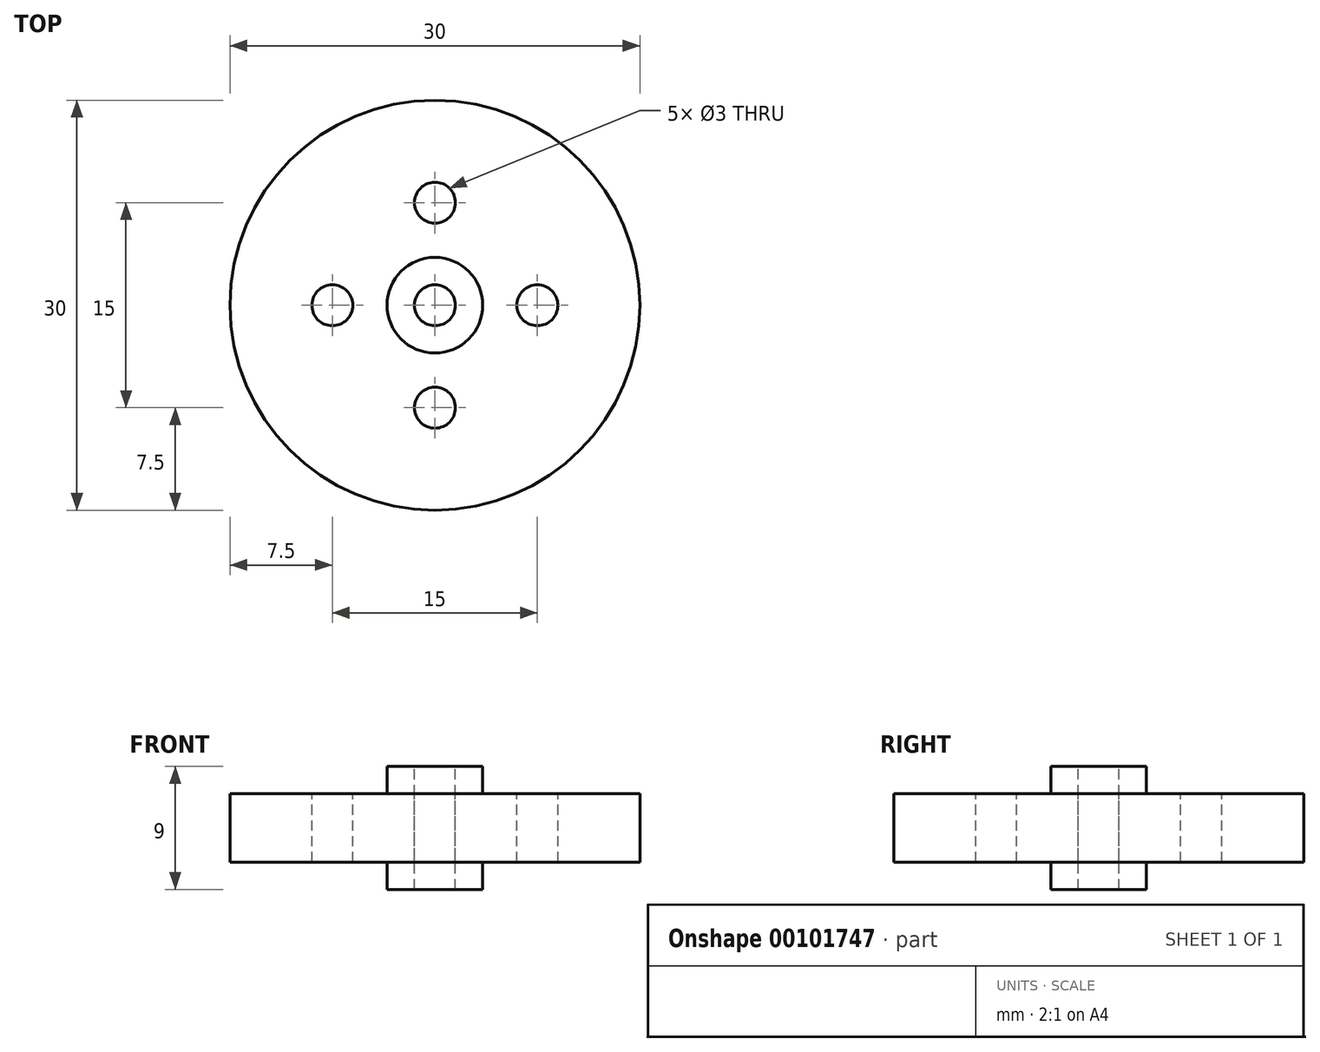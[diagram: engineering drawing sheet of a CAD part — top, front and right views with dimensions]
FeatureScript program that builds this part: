
annotation { "Feature Type Name" : "Feature", "Feature Type Description" : "" }
export const myFeature = defineFeature(function(context is Context, id is Id, definition is map)
    precondition{}
    {
        {
            var Q0;
            Q0=qCreatedBy(makeId("Top.planeOp"),FACE);
            var sketch = newSketch(context, id + "F0", { "sketchPlane" : qUnion([Q0])});
            skCircle(sketch, "E0", {"center": v(0, 0) * mm, "radius": 15 * mm});
            skSolve(sketch);
        }
        {
            var Q0;
            Q0=qSketchRegion(id+"F0",true);
            extrude(context, id + "F1", {"entities" : qUnion([Q0]), "depth" : 5 * mm});
        }
        {
            var Q0;
            Q0=makeQuery(id+"F1.opExtrude","CAP_FACE",FACE,{"disambiguationData":[OSD([sQuery(id+"F0.wireOp",EDGE,"E0")])],"isStart":false});
            var sketch = newSketch(context, id + "F2", { "sketchPlane" : qUnion([Q0])});
            skLineSegment(sketch, "E1", {"start": v(0, 15) * mm, "end": v(0, 7.5) * mm});
            skCircle(sketch, "E2", {"center": v(0, 7.5) * mm, "radius": 1.5 * mm});
            skCircle(sketch, "E3.1.0", {"center": v(-7.5, 0) * mm, "radius": 1.5 * mm});
            skCircle(sketch, "E3.2.0", {"center": v(0, -7.5) * mm, "radius": 1.5 * mm});
            skCircle(sketch, "E3.3.0", {"center": v(7.5, 0) * mm, "radius": 1.5 * mm});
            skPoint(sketch, "E3.center", {"position": v(0, 0) * mm});
            skCircle(sketch, "E4", {"center": v(0, 0) * mm, "radius": 3.5 * mm});
            skSolve(sketch);
        }
        {
            var Q0;
            Q0=makeQuery(id+"F2.imprint","IMPRINT",FACE,{"disambiguationData":[TD([[makeQuery(id+"F2.imprint","IMPRINT",EDGE,{"derivedFrom":sQuery(id+"F2.wireOp",EDGE,"E4")}),1.0]])]});
            extrude(context, id + "F3", {"entities" : qUnion([Q0]), "operationType" : NewBodyOperationType.ADD, "depth" : 2 * mm});
        }
        {
            var Q0;
            Q0=makeQuery(id+"F2.imprint","IMPRINT",FACE,{"disambiguationData":[TD([[makeQuery(id+"F2.imprint","IMPRINT",EDGE,{"derivedFrom":sQuery(id+"F2.wireOp",EDGE,"E2")}),1.0]])]});
            var Q1;
            Q1=makeQuery(id+"F2.imprint","IMPRINT",FACE,{"disambiguationData":[TD([[makeQuery(id+"F2.imprint","IMPRINT",EDGE,{"derivedFrom":sQuery(id+"F2.wireOp",EDGE,"E3.1.0")}),1.0]])]});
            var Q2;
            Q2=makeQuery(id+"F2.imprint","IMPRINT",FACE,{"disambiguationData":[TD([[makeQuery(id+"F2.imprint","IMPRINT",EDGE,{"derivedFrom":sQuery(id+"F2.wireOp",EDGE,"E3.2.0")}),1.0]])]});
            var Q3;
            Q3=makeQuery(id+"F2.imprint","IMPRINT",FACE,{"disambiguationData":[TD([[makeQuery(id+"F2.imprint","IMPRINT",EDGE,{"derivedFrom":sQuery(id+"F2.wireOp",EDGE,"E3.3.0")}),1.0]])]});
            extrude(context, id + "F4", {"entities" : qUnion([Q0, Q1, Q2, Q3]), "operationType" : NewBodyOperationType.REMOVE, "oppositeDirection" : true, "depth" : 5 * mm});
        }
        {
            var Q0;
            Q0=makeQuery(id+"F3.opExtrude","CAP_FACE",FACE,{"disambiguationData":[OSD([sQuery(id+"F2.wireOp",EDGE,"E4")])],"isStart":false});
            var sketch = newSketch(context, id + "F5", { "sketchPlane" : qUnion([Q0])});
            skCircle(sketch, "E5", {"center": v(0, 0) * mm, "radius": 1.5 * mm});
            skSolve(sketch);
        }
        {
            var Q0;
            Q0=makeQuery(id+"F5.imprint","IMPRINT",FACE,{"disambiguationData":[TD([[makeQuery(id+"F5.imprint","IMPRINT",EDGE,{"derivedFrom":sQuery(id+"F5.wireOp",EDGE,"E5")}),1.0]])]});
            extrude(context, id + "F6", {"entities" : qUnion([Q0]), "operationType" : NewBodyOperationType.REMOVE, "oppositeDirection" : true, "depth" : 10 * mm});
        }
        {
            var Q0;
            Q0=makeQuery(id+"F1.opExtrude","SWEPT_BODY",BODY,{"disambiguationData":[OSD([sQuery(id+"F0.wireOp",EDGE,"E0")])]});
            transform(context, id + "F7", {"entities" : qUnion([Q0]), "transformType" : TransformType.TRANSLATION_3D, "dx" : 0 * mm, "dy" : 0 * mm, "dz" : 0 * mm, "makeCopy" : true});
        }
        {
            var Q0;
            Q0=makeQuery(id+"F1.opExtrude","CAP_FACE",FACE,{"disambiguationData":[OSD([sQuery(id+"F0.wireOp",EDGE,"E0")])],"isStart":true});
            var sketch = newSketch(context, id + "F8", { "sketchPlane" : qUnion([Q0])});
            skCircle(sketch, "E6", {"center": v(0, 0) * mm, "radius": 3.5 * mm});
            skSolve(sketch);
        }
        {
            var Q0;
            Q0=makeQuery(id+"F8.imprint","IMPRINT",FACE,{"disambiguationData":[TD([[makeQuery(id+"F8.imprint","IMPRINT",EDGE,{"derivedFrom":sQuery(id+"F8.wireOp",EDGE,"E6")}),1.0]])]});
            extrude(context, id + "F9", {"entities" : qUnion([Q0]), "operationType" : NewBodyOperationType.ADD, "depth" : 2 * mm});
        }
    });
